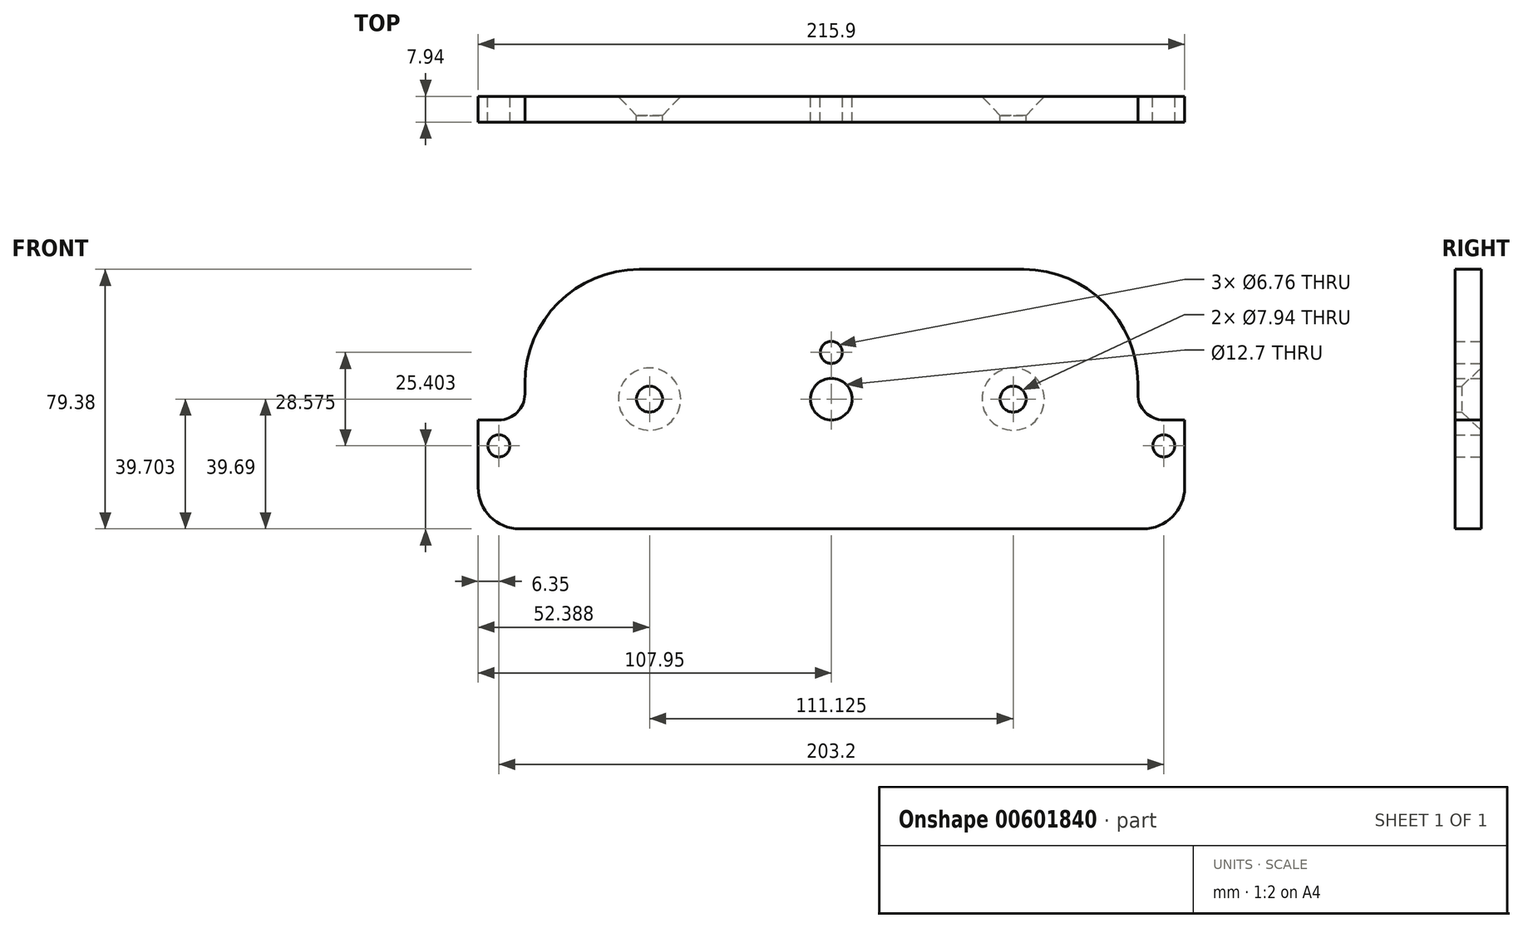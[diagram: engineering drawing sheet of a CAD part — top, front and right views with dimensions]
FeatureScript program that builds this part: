
annotation { "Feature Type Name" : "Feature", "Feature Type Description" : "" }
export const myFeature = defineFeature(function(context is Context, id is Id, definition is map)
    precondition{}
    {
        {
            var Q0;
            Q0=qCreatedBy(makeId("Front.planeOp"),FACE);
            var sketch = newSketch(context, id + "F0", { "sketchPlane" : qUnion([Q0])});
            skLineSegment(sketch, "E0", {"start": v(-107.95, -33.34) * mm, "end": v(107.95, -33.34) * mm});
            skLineSegment(sketch, "E1", {"start": v(107.95, -33.34) * mm, "end": v(107.95, 0) * mm});
            skLineSegment(sketch, "E2", {"start": v(107.95, 0) * mm, "end": v(93.66, 0) * mm});
            skLineSegment(sketch, "E3", {"start": v(93.66, 0) * mm, "end": v(93.66, 46.04) * mm});
            skLineSegment(sketch, "E4", {"start": v(93.66, 46.04) * mm, "end": v(-93.66, 46.04) * mm});
            skLineSegment(sketch, "E5", {"start": v(-93.66, 46.04) * mm, "end": v(-93.66, 0) * mm});
            skLineSegment(sketch, "E6", {"start": v(-93.66, 0) * mm, "end": v(-107.95, 0) * mm});
            skLineSegment(sketch, "E7", {"start": v(-107.95, -33.34) * mm, "end": v(-107.95, 0) * mm});
            skPoint(sketch, "E8", {"position": v(-101.6, -7.94) * mm});
            skPoint(sketch, "E9", {"position": v(101.6, -7.94) * mm});
            skPoint(sketch, "E10", {"position": v(0, 20.64) * mm});
            skPoint(sketch, "E11", {"position": v(0, 6.35) * mm});
            skPoint(sketch, "E12", {"position": v(55.56, 6.36) * mm});
            skPoint(sketch, "E13", {"position": v(-55.56, 6.36) * mm});
            skSolve(sketch);
        }
        {
            var Q0;
            Q0=makeQuery(id+"F0.imprint","IMPRINT",FACE,{"disambiguationData":[TD([[makeQuery(id+"F0.imprint","IMPRINT",EDGE,{"derivedFrom":sQuery(id+"F0.wireOp",EDGE,"E0")}),1.0]])]});
            extrude(context, id + "F1", {"entities" : qUnion([Q0]), "depth" : 7.94 * mm, "offsetDistance" : 25.4 * mm});
        }
        {
            var Q0;
            Q0=makeQuery(id+"F1.opExtrude","SWEPT_EDGE",EDGE,{"disambiguationData":[OSD([sQuery(id+"F0.wireOp",EDGE,"E4"),sQuery(id+"F0.wireOp",EDGE,"E5")])]});
            var Q1;
            Q1=makeQuery(id+"F1.opExtrude","SWEPT_EDGE",EDGE,{"disambiguationData":[OSD([sQuery(id+"F0.wireOp",EDGE,"E3"),sQuery(id+"F0.wireOp",EDGE,"E4")])]});
            fillet(context, id + "F2", {"entities" : qUnion([Q0, Q1]), "radius" : 34.92 * mm, "tangentPropagation" : true, "allowEdgeOverflow" : false});
        }
        {
            var Q0;
            Q0=makeQuery(id+"F1.opExtrude","SWEPT_EDGE",EDGE,{"disambiguationData":[OSD([sQuery(id+"F0.wireOp",EDGE,"E0"),sQuery(id+"F0.wireOp",EDGE,"E7")])]});
            var Q1;
            Q1=makeQuery(id+"F1.opExtrude","SWEPT_EDGE",EDGE,{"disambiguationData":[OSD([sQuery(id+"F0.wireOp",EDGE,"E0"),sQuery(id+"F0.wireOp",EDGE,"E1")])]});
            fillet(context, id + "F3", {"entities" : qUnion([Q0, Q1]), "radius" : 12.7 * mm, "tangentPropagation" : true, "allowEdgeOverflow" : false});
        }
        {
            var Q0;
            Q0=sQuery(id+"F0.wireOp",VERTEX,"E8");
            var Q1;
            Q1=sQuery(id+"F0.wireOp",VERTEX,"E9");
            var Q2;
            Q2=makeQuery(id+"F1.opExtrude","SWEPT_BODY",BODY,{"disambiguationData":[OSD([sQuery(id+"F0.wireOp",EDGE,"E0"),sQuery(id+"F0.wireOp",EDGE,"E1"),sQuery(id+"F0.wireOp",EDGE,"E2"),sQuery(id+"F0.wireOp",EDGE,"E3"),sQuery(id+"F0.wireOp",EDGE,"E4"),sQuery(id+"F0.wireOp",EDGE,"E5"),sQuery(id+"F0.wireOp",EDGE,"E6"),sQuery(id+"F0.wireOp",EDGE,"E7")])]});
            hole(context, id + "F4", {"style" : HoleStyle.SIMPLE, "endStyle" : HoleEndStyle.THROUGH, "oppositeDirection" : true, "standardTappedOrClearance" : lookupTablePath({ "standard" : "ANSI", "fit" : "Normal (ASME)", "size" : "1/4", "type" : "Clearance" }), "standardBlindInLast" : lookupTablePath({ "fit" : "Free", "standard" : "ANSI", "size" : "1/4", "type" : "Clearance" }), "holeDiameter" : 6.76 * mm, "majorDiameter" : 6.35 * mm, "isTappedThrough" : true, "tappedDepth" : 12.7 * mm, "tapClearance" : 3, "locations" : qUnion([Q0, Q1]), "scope" : qUnion([Q2])});
        }
        {
            var Q0;
            Q0=sQuery(id+"F0.wireOp",VERTEX,"E10");
            var Q1;
            Q1=makeQuery(id+"F1.opExtrude","SWEPT_BODY",BODY,{"disambiguationData":[OSD([sQuery(id+"F0.wireOp",EDGE,"E0"),sQuery(id+"F0.wireOp",EDGE,"E1"),sQuery(id+"F0.wireOp",EDGE,"E2"),sQuery(id+"F0.wireOp",EDGE,"E3"),sQuery(id+"F0.wireOp",EDGE,"E4"),sQuery(id+"F0.wireOp",EDGE,"E5"),sQuery(id+"F0.wireOp",EDGE,"E6"),sQuery(id+"F0.wireOp",EDGE,"E7")])]});
            hole(context, id + "F5", {"style" : HoleStyle.SIMPLE, "endStyle" : HoleEndStyle.THROUGH, "oppositeDirection" : true, "standardTappedOrClearance" : lookupTablePath({ "standard" : "ANSI", "fit" : "Normal (ASME)", "size" : "1/4", "type" : "Clearance" }), "standardBlindInLast" : lookupTablePath({ "fit" : "Free", "standard" : "ANSI", "size" : "1/4", "type" : "Clearance" }), "holeDiameter" : 6.76 * mm, "majorDiameter" : 6.35 * mm, "isTappedThrough" : true, "tappedDepth" : 12.7 * mm, "tapClearance" : 3, "locations" : qUnion([Q0]), "scope" : qUnion([Q1])});
        }
        {
            var Q0;
            Q0=sQuery(id+"F0.wireOp",VERTEX,"E11");
            var Q1;
            Q1=makeQuery(id+"F1.opExtrude","SWEPT_BODY",BODY,{"disambiguationData":[OSD([sQuery(id+"F0.wireOp",EDGE,"E0"),sQuery(id+"F0.wireOp",EDGE,"E1"),sQuery(id+"F0.wireOp",EDGE,"E2"),sQuery(id+"F0.wireOp",EDGE,"E3"),sQuery(id+"F0.wireOp",EDGE,"E4"),sQuery(id+"F0.wireOp",EDGE,"E5"),sQuery(id+"F0.wireOp",EDGE,"E6"),sQuery(id+"F0.wireOp",EDGE,"E7")])]});
            hole(context, id + "F6", {"style" : HoleStyle.SIMPLE, "endStyle" : HoleEndStyle.THROUGH, "oppositeDirection" : true, "holeDiameter" : 12.7 * mm, "majorDiameter" : 6.35 * mm, "isTappedThrough" : true, "tappedDepth" : 12.7 * mm, "tapClearance" : 3, "locations" : qUnion([Q0]), "scope" : qUnion([Q1])});
        }
        {
            var Q0;
            Q0=makeQuery(id+"F1.opExtrude","SWEPT_EDGE",EDGE,{"disambiguationData":[OSD([sQuery(id+"F0.wireOp",EDGE,"E5"),sQuery(id+"F0.wireOp",EDGE,"E6")])]});
            var Q1;
            Q1=makeQuery(id+"F1.opExtrude","SWEPT_EDGE",EDGE,{"disambiguationData":[OSD([sQuery(id+"F0.wireOp",EDGE,"E2"),sQuery(id+"F0.wireOp",EDGE,"E3")])]});
            fillet(context, id + "F7", {"entities" : qUnion([Q0, Q1]), "radius" : 7.94 * mm, "tangentPropagation" : true, "allowEdgeOverflow" : false});
        }
        {
            var Q0;
            Q0=sQuery(id+"F0.wireOp",VERTEX,"E13");
            var Q1;
            Q1=sQuery(id+"F0.wireOp",VERTEX,"E12");
            var Q2;
            Q2=makeQuery(id+"F1.opExtrude","SWEPT_BODY",BODY,{"disambiguationData":[OSD([sQuery(id+"F0.wireOp",EDGE,"E0"),sQuery(id+"F0.wireOp",EDGE,"E1"),sQuery(id+"F0.wireOp",EDGE,"E2"),sQuery(id+"F0.wireOp",EDGE,"E3"),sQuery(id+"F0.wireOp",EDGE,"E4"),sQuery(id+"F0.wireOp",EDGE,"E5"),sQuery(id+"F0.wireOp",EDGE,"E6"),sQuery(id+"F0.wireOp",EDGE,"E7")])]});
            hole(context, id + "F8", {"style" : HoleStyle.C_SINK, "endStyle" : HoleEndStyle.THROUGH, "oppositeDirection" : true, "holeDiameter" : 7.94 * mm, "cSinkDiameter" : 19.05 * mm, "cSinkAngle" : 86 * degree, "majorDiameter" : 6.35 * mm, "isTappedThrough" : true, "tappedDepth" : 12.7 * mm, "tapClearance" : 3, "locations" : qUnion([Q0, Q1]), "scope" : qUnion([Q2])});
        }
    });
